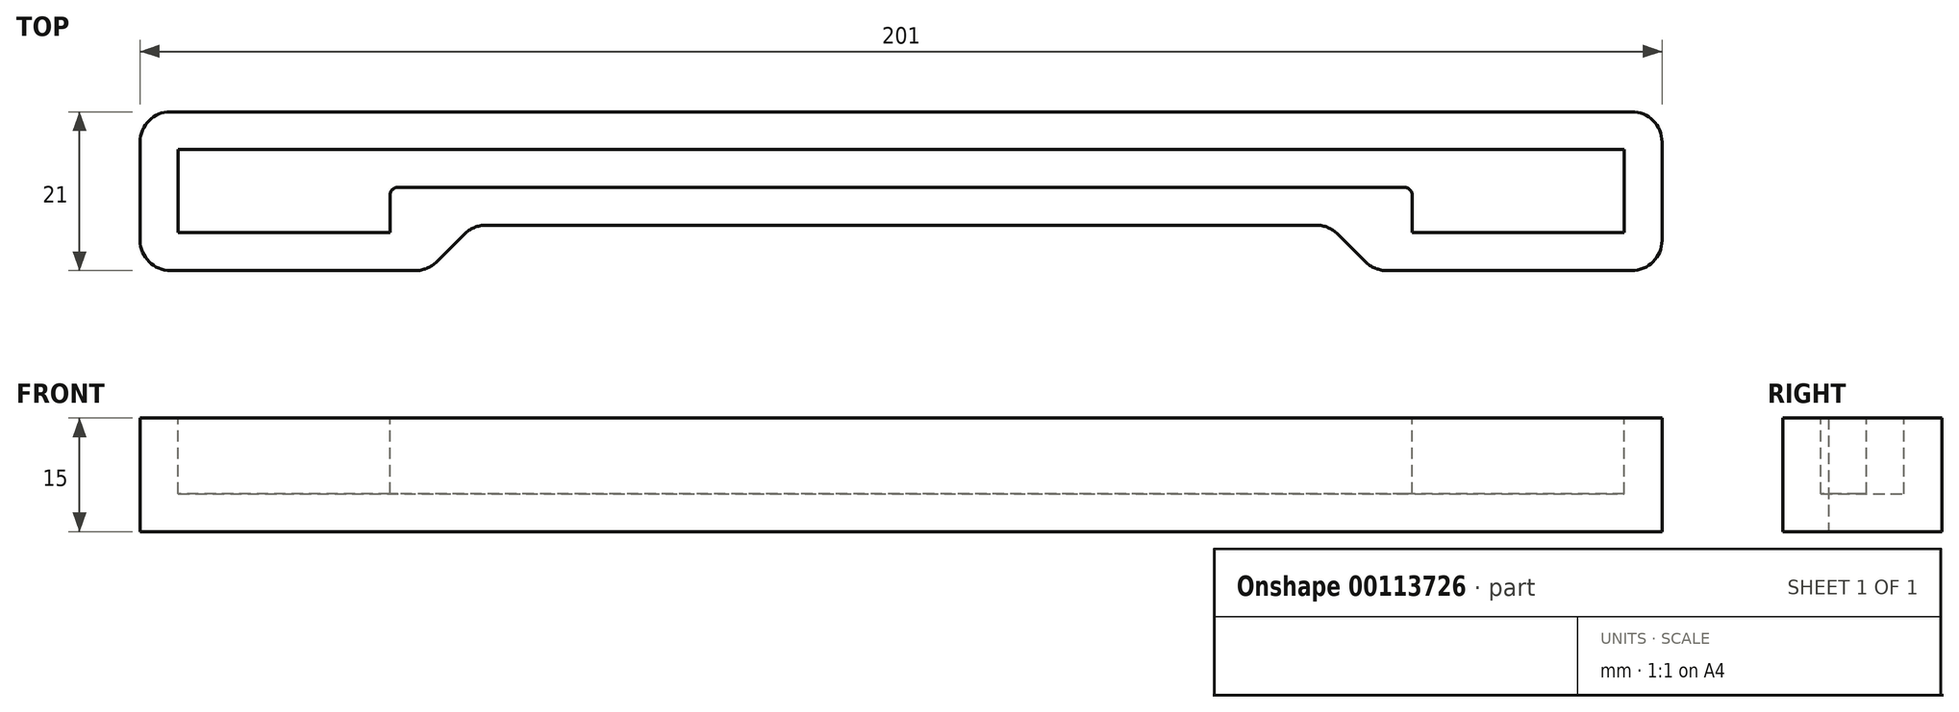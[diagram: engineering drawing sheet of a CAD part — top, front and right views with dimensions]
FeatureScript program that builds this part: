
annotation { "Feature Type Name" : "Feature", "Feature Type Description" : "" }
export const myFeature = defineFeature(function(context is Context, id is Id, definition is map)
    precondition{}
    {
        {
            var Q0;
            Q0=qCreatedBy(makeId("Top.planeOp"),FACE);
            var sketch = newSketch(context, id + "F0", { "sketchPlane" : qUnion([Q0])});
            skLineSegment(sketch, "E0.bottom", {"start": v(-100.5, 21) * mm, "end": v(100.5, 21) * mm});
            skLineSegment(sketch, "E0.top", {"start": v(-100.5, 0) * mm, "end": v(100.5, 0) * mm});
            skLineSegment(sketch, "E0.left", {"start": v(-100.5, 21) * mm, "end": v(-100.5, 0) * mm});
            skLineSegment(sketch, "E0.right", {"start": v(100.5, 21) * mm, "end": v(100.5, 0) * mm});
            skLineSegment(sketch, "E1", {"start": v(-62.5, 0) * mm, "end": v(-56.5, 6) * mm});
            skLineSegment(sketch, "E2", {"start": v(-56.5, 6) * mm, "end": v(56.5, 6) * mm});
            skLineSegment(sketch, "E3", {"start": v(56.5, 6) * mm, "end": v(62.5, 0) * mm});
            skSolve(sketch);
        }
        {
            var Q0;
            Q0=makeQuery(id+"F0.imprint","IMPRINT",FACE,{"disambiguationData":[TD([[makeQuery(id+"F0.imprint","IMPRINT",EDGE,{"derivedFrom":sQuery(id+"F0.wireOp",EDGE,"E0.bottom")}),-1.0]])]});
            extrude(context, id + "F1", {"entities" : qUnion([Q0]), "depth" : 15 * mm});
        }
        {
            var Q0;
            Q0=makeQuery(id+"F1.opExtrude","CAP_FACE",FACE,{"disambiguationData":[OSD([sQuery(id+"F0.wireOp",EDGE,"E0.bottom"),sQuery(id+"F0.wireOp",EDGE,"E0.top"),sQuery(id+"F0.wireOp",EDGE,"E0.left"),sQuery(id+"F0.wireOp",EDGE,"E0.right"),sQuery(id+"F0.wireOp",EDGE,"E1"),sQuery(id+"F0.wireOp",EDGE,"E2"),sQuery(id+"F0.wireOp",EDGE,"E3")])],"isStart":false});
            var sketch = newSketch(context, id + "F2", { "sketchPlane" : qUnion([Q0])});
            skLineSegment(sketch, "E4", {"start": v(-95.5, 16) * mm, "end": v(95.5, 16) * mm});
            skLineSegment(sketch, "E5", {"start": v(95.5, 16) * mm, "end": v(95.5, 5) * mm});
            skLineSegment(sketch, "E6", {"start": v(95.5, 5) * mm, "end": v(67.5, 5) * mm});
            skLineSegment(sketch, "E7", {"start": v(67.5, 5) * mm, "end": v(67.5, 11) * mm});
            skLineSegment(sketch, "E8", {"start": v(67.5, 11) * mm, "end": v(-67.5, 11) * mm});
            skLineSegment(sketch, "E9", {"start": v(-67.5, 11) * mm, "end": v(-67.5, 5) * mm});
            skLineSegment(sketch, "E10", {"start": v(-67.5, 5) * mm, "end": v(-95.5, 5) * mm});
            skLineSegment(sketch, "E11", {"start": v(-95.5, 5) * mm, "end": v(-95.5, 16) * mm});
            skSolve(sketch);
        }
        {
            var Q0;
            Q0=makeQuery(id+"F2.imprint","IMPRINT",FACE,{"disambiguationData":[TD([[makeQuery(id+"F2.imprint","IMPRINT",EDGE,{"derivedFrom":sQuery(id+"F2.wireOp",EDGE,"E4")}),-1.0]])]});
            extrude(context, id + "F3", {"entities" : qUnion([Q0]), "operationType" : NewBodyOperationType.REMOVE, "oppositeDirection" : true, "depth" : 10 * mm});
        }
        {
            var Q0;
            Q0=makeQuery(id+"F3.boolean.opBoolean","COPY",EDGE,{"derivedFrom":makeQuery(id+"F3.opExtrude","SWEPT_EDGE",EDGE,{"disambiguationData":[OSD([sQuery(id+"F2.wireOp",EDGE,"E7"),sQuery(id+"F2.wireOp",EDGE,"E8")])]})});
            var Q1;
            Q1=makeQuery(id+"F3.boolean.opBoolean","COPY",EDGE,{"derivedFrom":makeQuery(id+"F3.opExtrude","SWEPT_EDGE",EDGE,{"disambiguationData":[OSD([sQuery(id+"F2.wireOp",EDGE,"E8"),sQuery(id+"F2.wireOp",EDGE,"E9")])]})});
            fillet(context, id + "F4", {"entities" : qUnion([Q0, Q1]), "radius" : 1 * mm, "tangentPropagation" : true, "allowEdgeOverflow" : false});
        }
        {
            var Q0;
            Q0=makeQuery(id+"F1.opExtrude","SWEPT_EDGE",EDGE,{"disambiguationData":[OSD([sQuery(id+"F0.wireOp",EDGE,"E0.top"),sQuery(id+"F0.wireOp",EDGE,"E1")])]});
            var Q1;
            Q1=makeQuery(id+"F1.opExtrude","SWEPT_EDGE",EDGE,{"disambiguationData":[OSD([sQuery(id+"F0.wireOp",EDGE,"E1"),sQuery(id+"F0.wireOp",EDGE,"E2")])]});
            var Q2;
            Q2=makeQuery(id+"F1.opExtrude","SWEPT_EDGE",EDGE,{"disambiguationData":[OSD([sQuery(id+"F0.wireOp",EDGE,"E2"),sQuery(id+"F0.wireOp",EDGE,"E3")])]});
            var Q3;
            Q3=makeQuery(id+"F1.opExtrude","SWEPT_EDGE",EDGE,{"disambiguationData":[OSD([sQuery(id+"F0.wireOp",EDGE,"E0.top"),sQuery(id+"F0.wireOp",EDGE,"E3")])]});
            var Q4;
            Q4=makeQuery(id+"F1.opExtrude","SWEPT_EDGE",EDGE,{"disambiguationData":[OSD([sQuery(id+"F0.wireOp",EDGE,"E0.top"),sQuery(id+"F0.wireOp",EDGE,"E0.left")])]});
            var Q5;
            Q5=makeQuery(id+"F1.opExtrude","SWEPT_EDGE",EDGE,{"disambiguationData":[OSD([sQuery(id+"F0.wireOp",EDGE,"E0.bottom"),sQuery(id+"F0.wireOp",EDGE,"E0.left")])]});
            var Q6;
            Q6=makeQuery(id+"F1.opExtrude","SWEPT_EDGE",EDGE,{"disambiguationData":[OSD([sQuery(id+"F0.wireOp",EDGE,"E0.bottom"),sQuery(id+"F0.wireOp",EDGE,"E0.right")])]});
            var Q7;
            Q7=makeQuery(id+"F1.opExtrude","SWEPT_EDGE",EDGE,{"disambiguationData":[OSD([sQuery(id+"F0.wireOp",EDGE,"E0.top"),sQuery(id+"F0.wireOp",EDGE,"E0.right")])]});
            fillet(context, id + "F5", {"entities" : qUnion([Q0, Q1, Q2, Q3, Q4, Q5, Q6, Q7]), "radius" : 4 * mm, "tangentPropagation" : true, "allowEdgeOverflow" : false});
        }
    });
